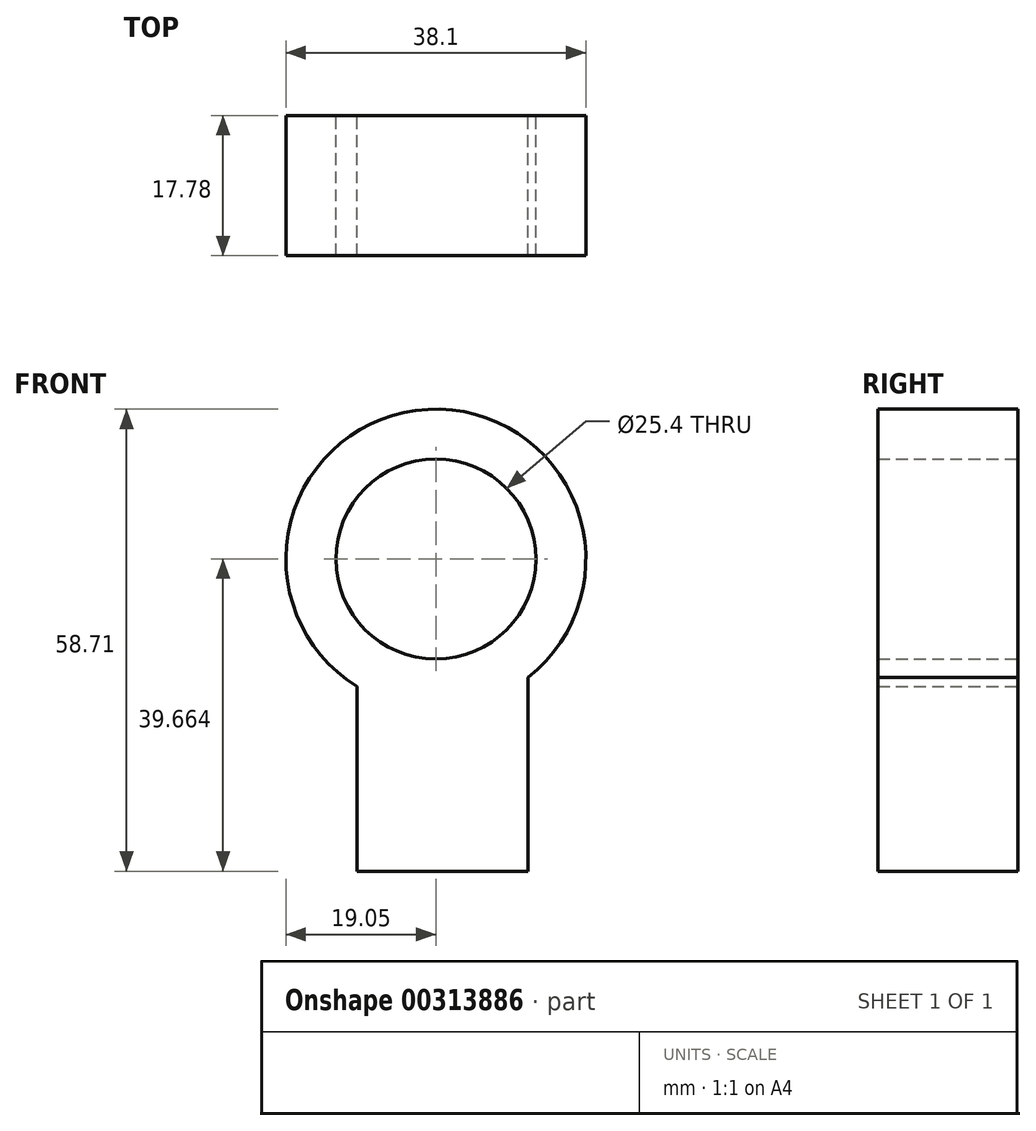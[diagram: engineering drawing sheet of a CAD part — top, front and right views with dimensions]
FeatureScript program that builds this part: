
annotation { "Feature Type Name" : "Feature", "Feature Type Description" : "" }
export const myFeature = defineFeature(function(context is Context, id is Id, definition is map)
    precondition{}
    {
        {
            var Q0;
            Q0=qCreatedBy(makeId("Front.planeOp"),FACE);
            var sketch = newSketch(context, id + "F0", { "sketchPlane" : qUnion([Q0])});
            skCircle(sketch, "E0", {"center": v(0, 43.27) * mm, "radius": 19.05 * mm});
            skLineSegment(sketch, "E1.bottom", {"start": v(-10.03, 29) * mm, "end": v(11.7, 29) * mm});
            skLineSegment(sketch, "E1.top", {"start": v(-10.03, 3.6) * mm, "end": v(11.7, 3.6) * mm});
            skLineSegment(sketch, "E1.left", {"start": v(-10.03, 29) * mm, "end": v(-10.03, 3.6) * mm});
            skLineSegment(sketch, "E1.right", {"start": v(11.7, 29) * mm, "end": v(11.7, 3.6) * mm});
            skCircle(sketch, "E2", {"center": v(0, 43.27) * mm, "radius": 12.7 * mm});
            skSolve(sketch);
        }
        {
            var Q0;
            Q0 = qSketchRegion(id + "F0", true);
            extrude(context, id + "F1", {"entities" : qUnion([Q0]), "depth" : 17.78 * mm});
        }
    });
